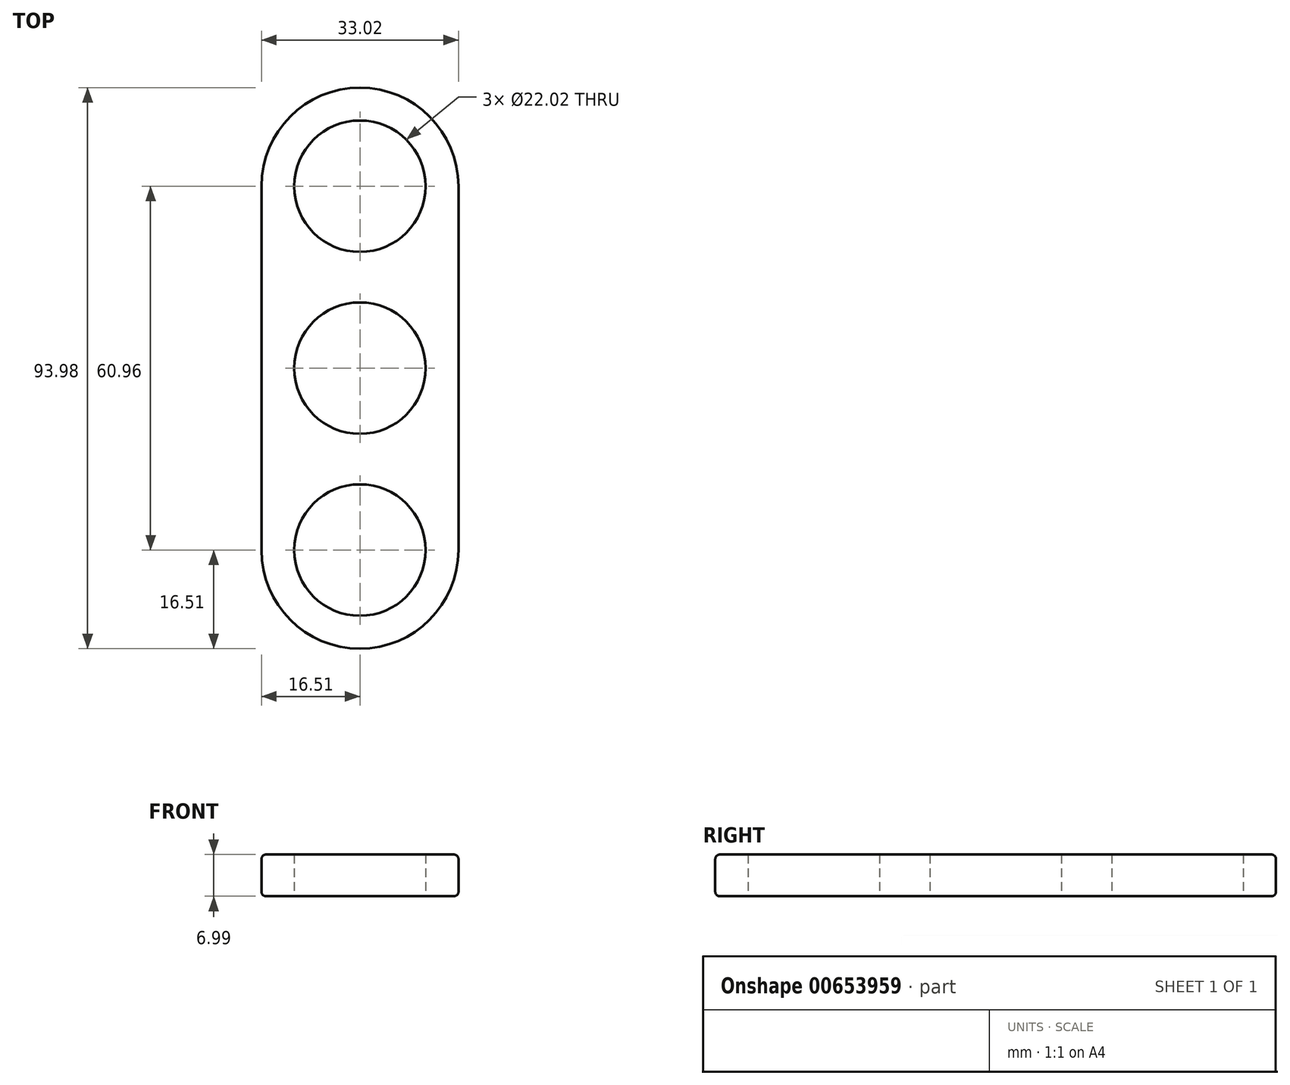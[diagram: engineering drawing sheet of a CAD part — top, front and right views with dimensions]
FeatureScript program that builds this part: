
annotation { "Feature Type Name" : "Feature", "Feature Type Description" : "" }
export const myFeature = defineFeature(function(context is Context, id is Id, definition is map)
    precondition{}
    {
        {
            var Q0;
            Q0=qCreatedBy(makeId("Top.planeOp"),FACE);
            var sketch = newSketch(context, id + "F0", { "sketchPlane" : qUnion([Q0])});
            skCircle(sketch, "E0", {"center": v(0, 0) * mm, "radius": 11.01 * mm});
            skCircle(sketch, "E1", {"center": v(0, 30.48) * mm, "radius": 11.01 * mm});
            skCircle(sketch, "E2", {"center": v(0, -30.48) * mm, "radius": 11.01 * mm});
            skLineSegment(sketch, "E3", {"start": v(0, 30.48) * mm, "end": v(0, 0) * mm});
            skLineSegment(sketch, "E4", {"start": v(0, 0) * mm, "end": v(0, -30.48) * mm});
            skCircle(sketch, "E5", {"center": v(0, 30.48) * mm, "radius": 16.51 * mm});
            skCircle(sketch, "E6", {"center": v(0, -30.48) * mm, "radius": 16.51 * mm});
            skLineSegment(sketch, "E7", {"start": v(-16.51, 30.48) * mm, "end": v(-16.5, -30.48) * mm});
            skLineSegment(sketch, "E8", {"start": v(16.51, 30.48) * mm, "end": v(16.51, -30.48) * mm});
            skSolve(sketch);
        }
        {
            var Q0;
            Q0 = qSketchRegion(id + "F0", true);
            extrude(context, id + "F1", {"entities" : qUnion([Q0]), "depth" : 7 * mm, "offsetDistance" : 25.4 * mm});
        }
        {
            var Q0;
            Q0=makeQuery(id+"F1.opExtrude","CAP_EDGE",EDGE,{"disambiguationData":[OSD([sQuery(id+"F0.wireOp",EDGE,"E8")])],"isStart":false});
            fillet(context, id + "F2", {"entities" : qUnion([Q0]), "radius" : 0.76 * mm, "tangentPropagation" : true, "allowEdgeOverflow" : false});
        }
        {
            var Q0;
            Q0=makeQuery(id+"F1.opExtrude","CAP_EDGE",EDGE,{"disambiguationData":[OSD([sQuery(id+"F0.wireOp",EDGE,"E6")])],"isStart":true});
            var Q1;
            Q1=makeQuery(id+"F1.opExtrude","CAP_EDGE",EDGE,{"disambiguationData":[OSD([sQuery(id+"F0.wireOp",EDGE,"E8")])],"isStart":true});
            var Q2;
            Q2=makeQuery(id+"F1.opExtrude","CAP_EDGE",EDGE,{"disambiguationData":[OSD([sQuery(id+"F0.wireOp",EDGE,"E5")])],"isStart":true});
            var Q3;
            Q3=makeQuery(id+"F1.opExtrude","CAP_EDGE",EDGE,{"disambiguationData":[OSD([sQuery(id+"F0.wireOp",EDGE,"E7")])],"isStart":true});
            fillet(context, id + "F3", {"entities" : qUnion([Q0, Q1, Q2, Q3]), "radius" : 0.76 * mm, "tangentPropagation" : true, "allowEdgeOverflow" : false});
        }
    });
